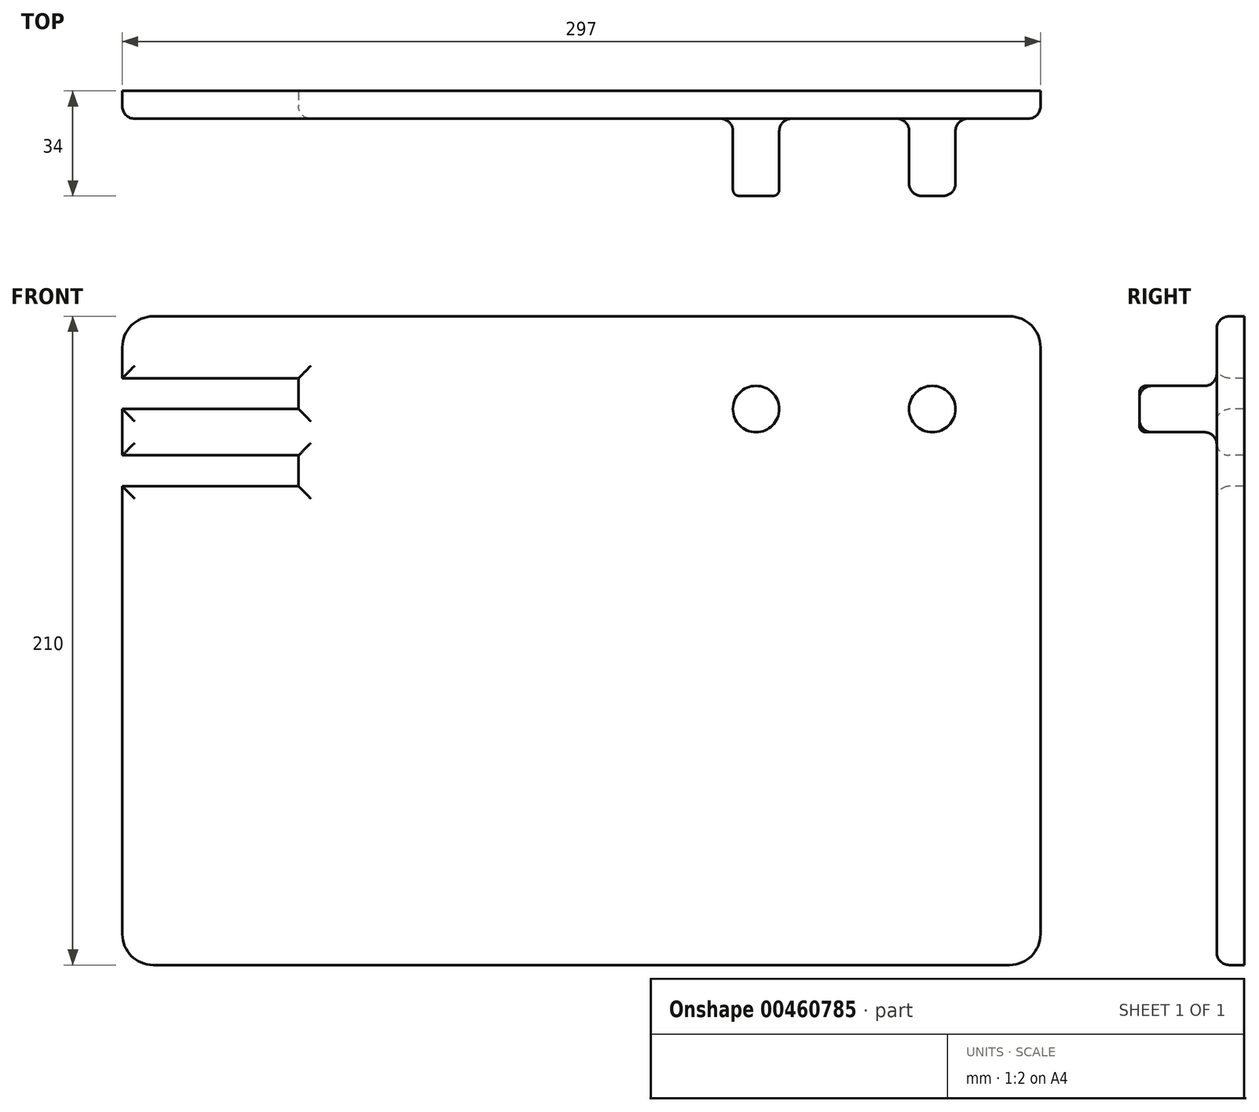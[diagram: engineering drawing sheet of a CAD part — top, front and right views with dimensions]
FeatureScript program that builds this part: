
annotation { "Feature Type Name" : "Feature", "Feature Type Description" : "" }
export const myFeature = defineFeature(function(context is Context, id is Id, definition is map)
    precondition{}
    {
        {
            var Q0;
            Q0=qCreatedBy(makeId("Front.planeOp"),FACE);
            var sketch = newSketch(context, id + "F0", { "sketchPlane" : qUnion([Q0])});
            skLineSegment(sketch, "E0.bottom", {"start": v(-45.74, 190.8) * mm, "end": v(231.26, 190.8) * mm});
            skLineSegment(sketch, "E0.top", {"start": v(-45.74, -19.2) * mm, "end": v(231.26, -19.2) * mm});
            skLineSegment(sketch, "E0.left", {"start": v(-55.74, 180.8) * mm, "end": v(-55.74, -9.2) * mm});
            skLineSegment(sketch, "E0.right", {"start": v(241.26, 180.8) * mm, "end": v(241.26, -9.2) * mm});
            skPoint(sketch, "E1.visualSharp", {"position": v(-55.74, 190.8) * mm});
            skArc(sketch, "E1.filletArc", {"start": v(-45.74, 190.8) * mm, "mid": v(-52.81, 187.88) * mm, "end": v(-55.74, 180.8) * mm});
            skPoint(sketch, "E2.visualSharp", {"position": v(241.26, 190.8) * mm});
            skArc(sketch, "E2.filletArc", {"start": v(241.26, 180.8) * mm, "mid": v(238.33, 187.88) * mm, "end": v(231.26, 190.8) * mm});
            skPoint(sketch, "E3.visualSharp", {"position": v(241.26, -19.2) * mm});
            skArc(sketch, "E3.filletArc", {"start": v(231.26, -19.2) * mm, "mid": v(238.33, -16.27) * mm, "end": v(241.26, -9.2) * mm});
            skPoint(sketch, "E4.visualSharp", {"position": v(-55.74, -19.2) * mm});
            skArc(sketch, "E4.filletArc", {"start": v(-55.74, -9.2) * mm, "mid": v(-52.81, -16.27) * mm, "end": v(-45.74, -19.2) * mm});
            skSolve(sketch);
        }
        {
            var Q0;
            Q0=makeQuery(id+"F0.imprint","IMPRINT",FACE,{"disambiguationData":[TD([[makeQuery(id+"F0.imprint","IMPRINT",EDGE,{"derivedFrom":sQuery(id+"F0.wireOp",EDGE,"E0.bottom")}),-1.0]])]});
            extrude(context, id + "F1", {"entities" : qUnion([Q0]), "depth" : 9 * mm});
        }
        {
            var Q0;
            Q0=makeQuery(id+"F1.opExtrude","CAP_FACE",FACE,{"disambiguationData":[OSD([sQuery(id+"F0.wireOp",EDGE,"E0.bottom"),sQuery(id+"F0.wireOp",EDGE,"E0.top"),sQuery(id+"F0.wireOp",EDGE,"E0.left"),sQuery(id+"F0.wireOp",EDGE,"E0.right"),sQuery(id+"F0.wireOp",EDGE,"E1.filletArc"),sQuery(id+"F0.wireOp",EDGE,"E2.filletArc"),sQuery(id+"F0.wireOp",EDGE,"E3.filletArc"),sQuery(id+"F0.wireOp",EDGE,"E4.filletArc")])],"isStart":false});
            var sketch = newSketch(context, id + "F2", { "sketchPlane" : qUnion([Q0])});
            skCircle(sketch, "E5", {"center": v(149.26, 160.8) * mm, "radius": 7.5 * mm});
            skCircle(sketch, "E6", {"center": v(206.26, 160.8) * mm, "radius": 7.5 * mm});
            skSolve(sketch);
        }
        {
            var Q0;
            Q0 = qSketchRegion(id + "F2", true);
            extrude(context, id + "F3", {"entities" : qUnion([Q0]), "operationType" : NewBodyOperationType.ADD, "depth" : 25 * mm});
        }
        {
            var Q0;
            Q0=makeQuery(id+"F1.opExtrude","CAP_FACE",FACE,{"disambiguationData":[OSD([sQuery(id+"F0.wireOp",EDGE,"E0.bottom"),sQuery(id+"F0.wireOp",EDGE,"E0.top"),sQuery(id+"F0.wireOp",EDGE,"E0.left"),sQuery(id+"F0.wireOp",EDGE,"E0.right"),sQuery(id+"F0.wireOp",EDGE,"E1.filletArc"),sQuery(id+"F0.wireOp",EDGE,"E2.filletArc"),sQuery(id+"F0.wireOp",EDGE,"E3.filletArc"),sQuery(id+"F0.wireOp",EDGE,"E4.filletArc")])],"isStart":false});
            var sketch = newSketch(context, id + "F4", { "sketchPlane" : qUnion([Q0])});
            skLineSegment(sketch, "E7.bottom", {"start": v(-55.74, 170.8) * mm, "end": v(1.26, 170.8) * mm});
            skLineSegment(sketch, "E7.top", {"start": v(-55.74, 160.8) * mm, "end": v(1.26, 160.8) * mm});
            skLineSegment(sketch, "E7.left", {"start": v(-55.74, 170.8) * mm, "end": v(-55.74, 160.8) * mm});
            skLineSegment(sketch, "E7.right", {"start": v(1.26, 170.8) * mm, "end": v(1.26, 160.8) * mm});
            skLineSegment(sketch, "E8.bottom", {"start": v(-55.74, 145.8) * mm, "end": v(1.26, 145.8) * mm});
            skLineSegment(sketch, "E8.top", {"start": v(-55.74, 135.8) * mm, "end": v(1.26, 135.8) * mm});
            skLineSegment(sketch, "E8.left", {"start": v(-55.74, 145.8) * mm, "end": v(-55.74, 135.8) * mm});
            skLineSegment(sketch, "E8.right", {"start": v(1.26, 145.8) * mm, "end": v(1.26, 135.8) * mm});
            skSolve(sketch);
        }
        {
            var Q0;
            Q0=makeQuery(id+"F4.imprint","IMPRINT",FACE,{"disambiguationData":[TD([[makeQuery(id+"F4.imprint","IMPRINT",EDGE,{"derivedFrom":sQuery(id+"F4.wireOp",EDGE,"E7.bottom")}),-1.0]])]});
            var Q1;
            Q1=makeQuery(id+"F4.imprint","IMPRINT",FACE,{"disambiguationData":[TD([[makeQuery(id+"F4.imprint","IMPRINT",EDGE,{"derivedFrom":sQuery(id+"F4.wireOp",EDGE,"E8.bottom")}),-1.0]])]});
            extrude(context, id + "F5", {"entities" : qUnion([Q0, Q1]), "operationType" : NewBodyOperationType.REMOVE, "oppositeDirection" : true, "depth" : 25 * mm});
        }
        {
            var Q0;
            Q0=makeQuery(id+"F3.opExtrude","CAP_FACE",FACE,{"disambiguationData":[OSD([sQuery(id+"F2.wireOp",EDGE,"E5")])],"isStart":false});
            fillet(context, id + "F6", {"entities" : qUnion([Q0]), "radius" : 2 * mm, "tangentPropagation" : true, "allowEdgeOverflow" : false});
        }
        {
            var Q0;
            Q0=makeQuery(id+"F3.opExtrude","CAP_EDGE",EDGE,{"disambiguationData":[OSD([sQuery(id+"F2.wireOp",EDGE,"E6")])],"isStart":false});
            fillet(context, id + "F7", {"entities" : qUnion([Q0]), "radius" : 4 * mm, "tangentPropagation" : true, "allowEdgeOverflow" : false});
        }
        {
            var Q0;
            Q0=makeQuery(id+"F3.opExtrude","CAP_FACE",FACE,{"disambiguationData":[OSD([sQuery(id+"F2.wireOp",EDGE,"E5")])],"isStart":false});
            var Q1;
            {var subQ0=sQuery(id+"F2.wireOp",EDGE,"E5");Q1=makeQuery(id+"F6.opFillet","BLEND_EDGE",EDGE,{"blendedFrom":[makeQuery(id+"F3.opExtrude","CAP_EDGE",EDGE,{"disambiguationData":[OSD([subQ0])],"isStart":false}),makeQuery(id+"F3.opExtrude","SWEPT_FACE",FACE,{"disambiguationData":[OSD([subQ0])]})],"blendedInto":[makeQuery(id+"F3.opExtrude","SWEPT_FACE",FACE,{"disambiguationData":[OSD([subQ0])]})]});}
            var Q2;
            Q2=makeQuery(id+"F1.opExtrude","CAP_FACE",FACE,{"disambiguationData":[OSD([sQuery(id+"F0.wireOp",EDGE,"E0.bottom"),sQuery(id+"F0.wireOp",EDGE,"E0.top"),sQuery(id+"F0.wireOp",EDGE,"E0.left"),sQuery(id+"F0.wireOp",EDGE,"E0.right"),sQuery(id+"F0.wireOp",EDGE,"E1.filletArc"),sQuery(id+"F0.wireOp",EDGE,"E2.filletArc"),sQuery(id+"F0.wireOp",EDGE,"E3.filletArc"),sQuery(id+"F0.wireOp",EDGE,"E4.filletArc")])],"isStart":false});
            fillet(context, id + "F8", {"entities" : qUnion([Q0, Q1, Q2]), "radius" : 4 * mm, "tangentPropagation" : true, "allowEdgeOverflow" : false});
        }
    });
